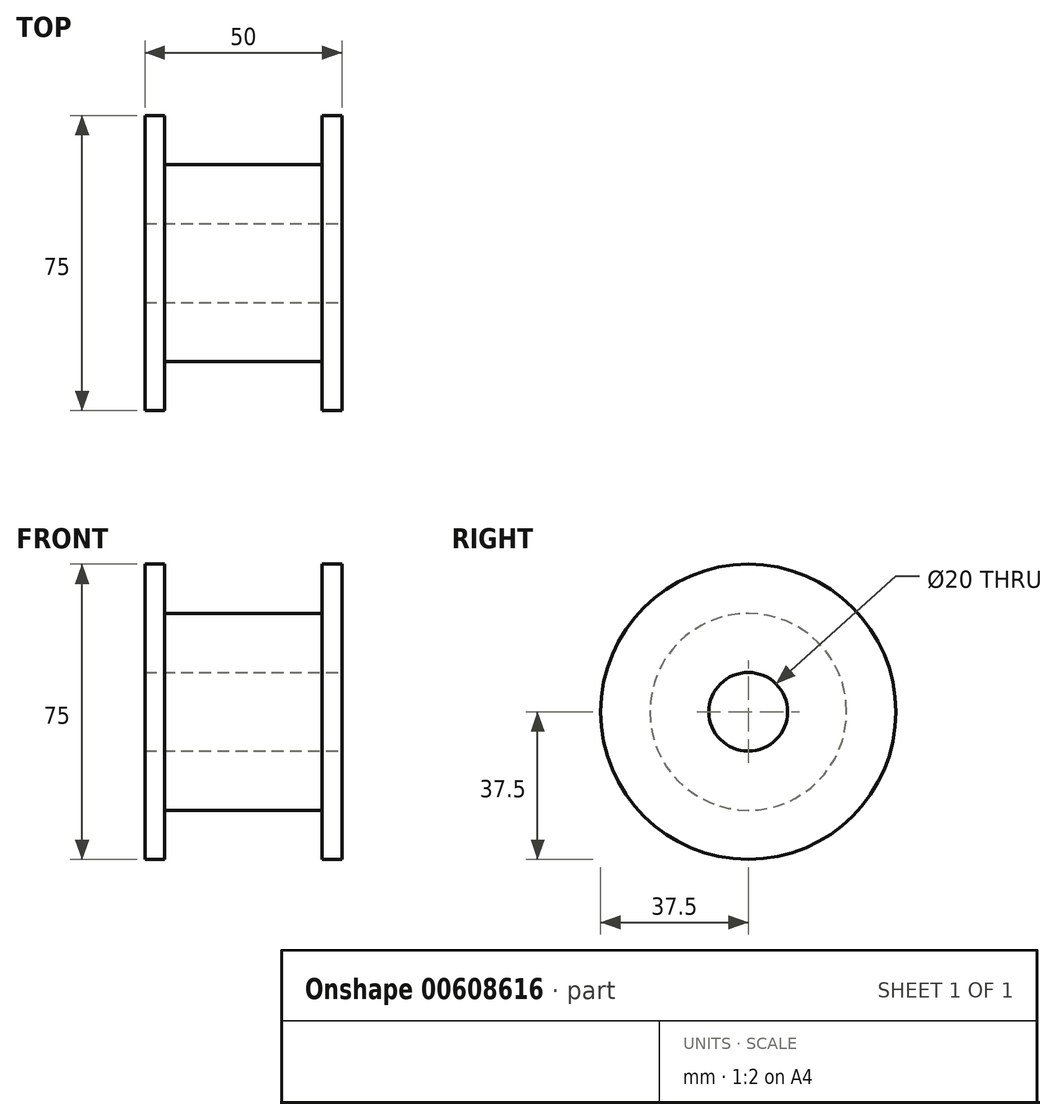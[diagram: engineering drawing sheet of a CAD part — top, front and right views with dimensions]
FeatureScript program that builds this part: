
annotation { "Feature Type Name" : "Feature", "Feature Type Description" : "" }
export const myFeature = defineFeature(function(context is Context, id is Id, definition is map)
    precondition{}
    {
        {
            var Q0;
            Q0=qCreatedBy(makeId("Right.planeOp"),FACE);
            var sketch = newSketch(context, id + "F0", { "sketchPlane" : qUnion([Q0])});
            skCircle(sketch, "E0", {"center": v(0, 0) * mm, "radius": 25 * mm});
            skSolve(sketch);
        }
        {
            var Q0;
            Q0=makeQuery(id+"F0.imprint","IMPRINT",FACE,{"disambiguationData":[TD([[makeQuery(id+"F0.imprint","IMPRINT",EDGE,{"derivedFrom":sQuery(id+"F0.wireOp",EDGE,"E0")}),1.0]])]});
            extrude(context, id + "F1", {"entities" : qUnion([Q0]), "depth" : 20 * mm, "offsetDistance" : 25 * mm});
        }
        {
            var Q0;
            Q0=makeQuery(id+"F1.opExtrude","CAP_FACE",FACE,{"disambiguationData":[OSD([sQuery(id+"F0.wireOp",EDGE,"E0")])],"isStart":false});
            var sketch = newSketch(context, id + "F2", { "sketchPlane" : qUnion([Q0])});
            skCircle(sketch, "E1", {"center": v(0, 0) * mm, "radius": 37.5 * mm});
            skSolve(sketch);
        }
        {
            var Q0;
            Q0=makeQuery(id+"F2.imprint","IMPRINT",FACE,{"disambiguationData":[TD([[makeQuery(id+"F2.imprint","IMPRINT",EDGE,{"derivedFrom":sQuery(id+"F2.wireOp",EDGE,"E1")}),1.0]])]});
            var Q1;
            Q1=makeQuery(id+"F2.imprint","IMPRINT",FACE,{"disambiguationData":[TD([[makeQuery(id+"F2.imprint","IMPRINT",EDGE,{"derivedFrom":makeQuery(id+"F1.opExtrude","CAP_EDGE",EDGE,{"disambiguationData":[OSD([sQuery(id+"F0.wireOp",EDGE,"E0")])],"isStart":false})}),1.0]])]});
            extrude(context, id + "F3", {"entities" : qUnion([Q0, Q1]), "operationType" : NewBodyOperationType.ADD, "depth" : 5 * mm, "offsetDistance" : 25 * mm});
        }
        {
            var Q0;
            Q0=makeQuery(id+"F1.opExtrude","SWEPT_BODY",BODY,{"disambiguationData":[OSD([sQuery(id+"F0.wireOp",EDGE,"E0")])]});
            var Q1;
            Q1=makeQuery(id+"F1.opExtrude","CAP_FACE",FACE,{"disambiguationData":[OSD([sQuery(id+"F0.wireOp",EDGE,"E0")])],"isStart":true});
            mirror(context, id + "F4", {"operationType" : NewBodyOperationType.ADD, "entities" : qUnion([Q0]), "mirrorPlane" : qUnion([Q1])});
        }
        {
            var Q0;
            Q0=makeQuery(id+"F3.opExtrude","CAP_FACE",FACE,{"disambiguationData":[OSD([sQuery(id+"F2.wireOp",EDGE,"E1")])],"isStart":false});
            var sketch = newSketch(context, id + "F5", { "sketchPlane" : qUnion([Q0])});
            skPoint(sketch, "E2", {"position": v(0, 0) * mm});
            skSolve(sketch);
        }
        {
            var Q0;
            Q0=sQuery(id+"F5.wireOp",VERTEX,"E2");
            var Q1;
            Q1=makeQuery(id+"F1.opExtrude","SWEPT_BODY",BODY,{"disambiguationData":[OSD([sQuery(id+"F0.wireOp",EDGE,"E0")])]});
            hole(context, id + "F6", {"style" : HoleStyle.SIMPLE, "endStyle" : HoleEndStyle.BLIND, "holeDiameter" : 20 * mm, "majorDiameter" : 5 * mm, "holeDepth" : 250 * mm, "isTappedThrough" : true, "tappedDepth" : 12 * mm, "tapClearance" : 3, "locations" : qUnion([Q0]), "scope" : qUnion([Q1])});
        }
    });
